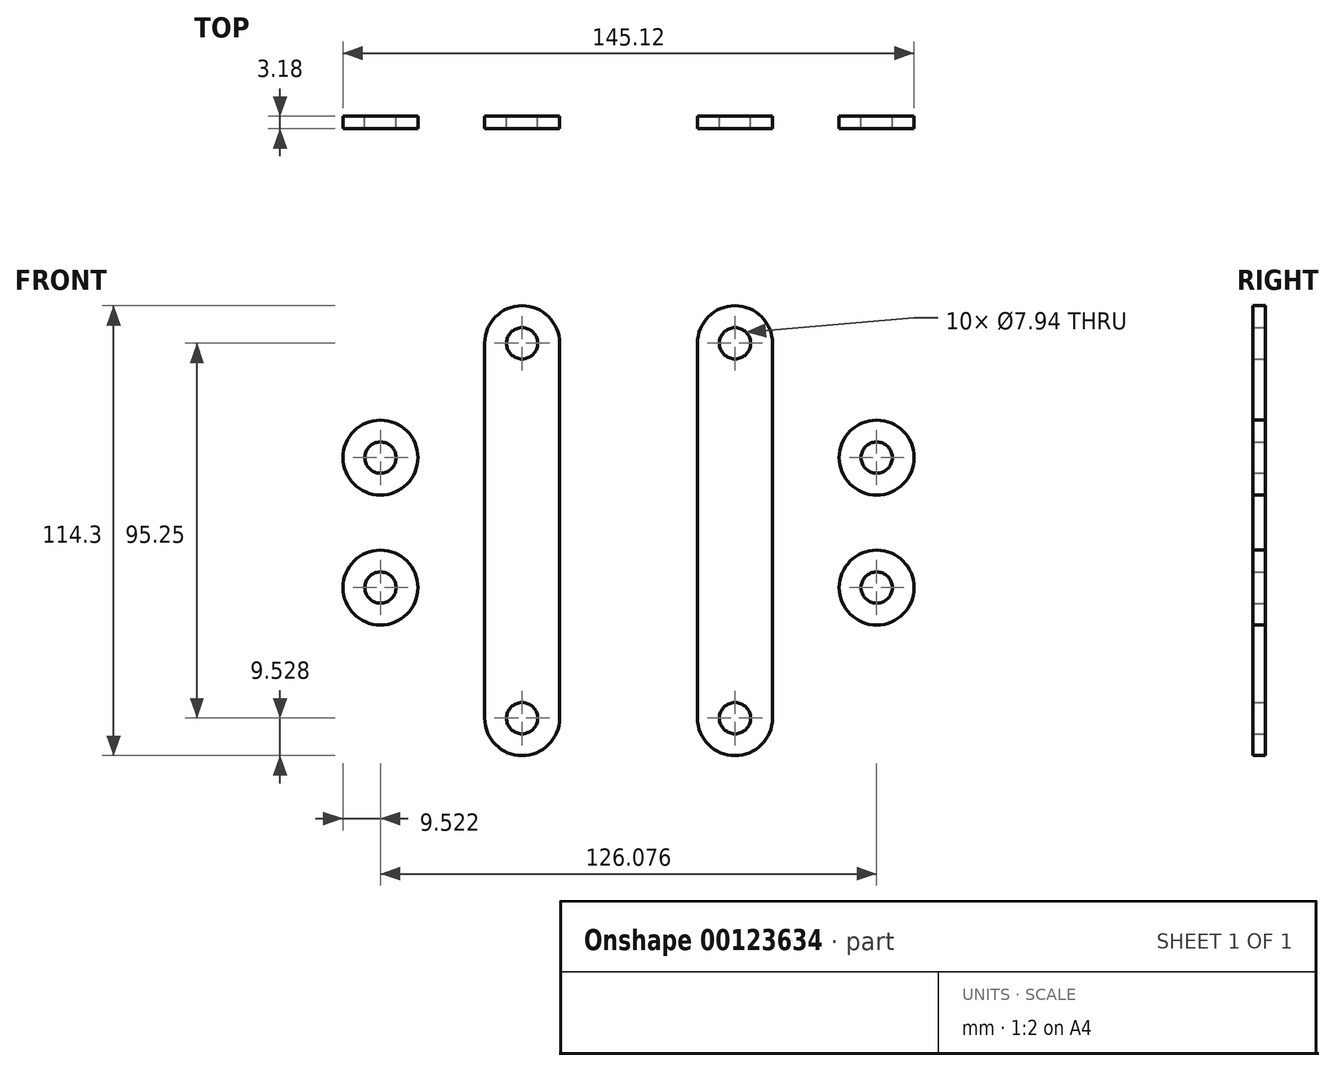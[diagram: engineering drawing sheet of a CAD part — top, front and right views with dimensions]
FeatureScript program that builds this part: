
annotation { "Feature Type Name" : "Feature", "Feature Type Description" : "" }
export const myFeature = defineFeature(function(context is Context, id is Id, definition is map)
    precondition{}
    {
        {
            var Q0;
            Q0=qCreatedBy(makeId("Front.planeOp"),FACE);
            var sketch = newSketch(context, id + "F0", { "sketchPlane" : qUnion([Q0])});
            skLineSegment(sketch, "E0", {"start": v(-36.56, 65.99) * mm, "end": v(-36.56, -29.26) * mm});
            skLineSegment(sketch, "E1", {"start": v(-17.51, -29.26) * mm, "end": v(-17.51, 65.99) * mm});
            skCircle(sketch, "E2", {"center": v(-63.04, 36.94) * mm, "radius": 9.53 * mm});
            skCircle(sketch, "E3", {"center": v(-63.04, 36.94) * mm, "radius": 3.97 * mm});
            skArc(sketch, "E4", {"start": v(-17.51, 65.99) * mm, "mid": v(-27.04, 75.51) * mm, "end": v(-36.56, 65.99) * mm});
            skArc(sketch, "E5", {"start": v(-36.56, -29.26) * mm, "mid": v(-27.04, -38.79) * mm, "end": v(-17.51, -29.26) * mm});
            skCircle(sketch, "E6", {"center": v(-27.04, 65.99) * mm, "radius": 3.97 * mm});
            skCircle(sketch, "E7", {"center": v(-27.04, -29.26) * mm, "radius": 3.97 * mm});
            skCircle(sketch, "E8", {"center": v(-63.04, 3.9) * mm, "radius": 3.97 * mm});
            skCircle(sketch, "E9", {"center": v(-63.04, 3.9) * mm, "radius": 9.53 * mm});
            skSolve(sketch);
        }
        {
            var Q0;
            Q0=makeQuery(id+"F0.imprint","IMPRINT",FACE,{"disambiguationData":[TD([[makeQuery(id+"F0.imprint","IMPRINT",EDGE,{"derivedFrom":sQuery(id+"F0.wireOp",EDGE,"E2")}),1.0]])]});
            var Q1;
            Q1=makeQuery(id+"F0.imprint","IMPRINT",FACE,{"disambiguationData":[TD([[makeQuery(id+"F0.imprint","IMPRINT",EDGE,{"derivedFrom":sQuery(id+"F0.wireOp",EDGE,"E8")}),-1.0]])]});
            var Q2;
            Q2=makeQuery(id+"F0.imprint","IMPRINT",FACE,{"disambiguationData":[TD([[makeQuery(id+"F0.imprint","IMPRINT",EDGE,{"derivedFrom":sQuery(id+"F0.wireOp",EDGE,"E0")}),1.0]])]});
            extrude(context, id + "F1", {"entities" : qUnion([Q0, Q1, Q2]), "depth" : 3.17 * mm});
        }
        {
            var Q0;
            Q0=makeQuery(id+"F1.opExtrude","SWEPT_BODY",BODY,{"disambiguationData":[OSD([sQuery(id+"F0.wireOp",EDGE,"E0"),sQuery(id+"F0.wireOp",EDGE,"E1"),sQuery(id+"F0.wireOp",EDGE,"UyuT9NgJ-HcHq-d4uN-E2Ay-fanq5567FBoP"),sQuery(id+"F0.wireOp",EDGE,"T3Yw2ueC-DSDP-vsul-hjrp-Bt92uGHRINVA"),sQuery(id+"F0.wireOp",EDGE,"kJNG0Jya-Q8As-0qdW-NQPh-vUQlsZO2qSjk"),sQuery(id+"F0.wireOp",EDGE,"HjnoBiv2-EU4K-6Lsv-dbCZ-xJGu657PI36A")])]});
            var Q1;
            Q1=qCreatedBy(makeId("Right.planeOp"),FACE);
            mirror(context, id + "F2", {"entities" : qUnion([Q0]), "mirrorPlane" : qUnion([Q1])});
        }
        {
            var Q0;
            Q0=makeQuery(id+"F0.imprint","IMPRINT",FACE,{"disambiguationData":[TD([[makeQuery(id+"F0.imprint","IMPRINT",EDGE,{"derivedFrom":sQuery(id+"F0.wireOp",EDGE,"E2")}),1.0]])]});
            var Q1;
            Q1=makeQuery(id+"F0.imprint","IMPRINT",FACE,{"disambiguationData":[TD([[makeQuery(id+"F0.imprint","IMPRINT",EDGE,{"derivedFrom":sQuery(id+"F0.wireOp",EDGE,"E8")}),-1.0]])]});
            extrude(context, id + "F3", {"entities" : qUnion([Q0, Q1]), "depth" : 3.17 * mm});
        }
        {
            var Q0;
            Q0=makeQuery(id+"F3.opExtrude","SWEPT_BODY",BODY,{"disambiguationData":[OSD([sQuery(id+"F0.wireOp",EDGE,"E2"),sQuery(id+"F0.wireOp",EDGE,"E3")])]});
            var Q1;
            Q1=makeQuery(id+"F3.opExtrude","SWEPT_BODY",BODY,{"disambiguationData":[OSD([sQuery(id+"F0.wireOp",EDGE,"E8"),sQuery(id+"F0.wireOp",EDGE,"E9")])]});
            var Q2;
            Q2=qCreatedBy(makeId("Right.planeOp"),FACE);
            mirror(context, id + "F4", {"entities" : qUnion([Q0, Q1]), "mirrorPlane" : qUnion([Q2])});
        }
    });
